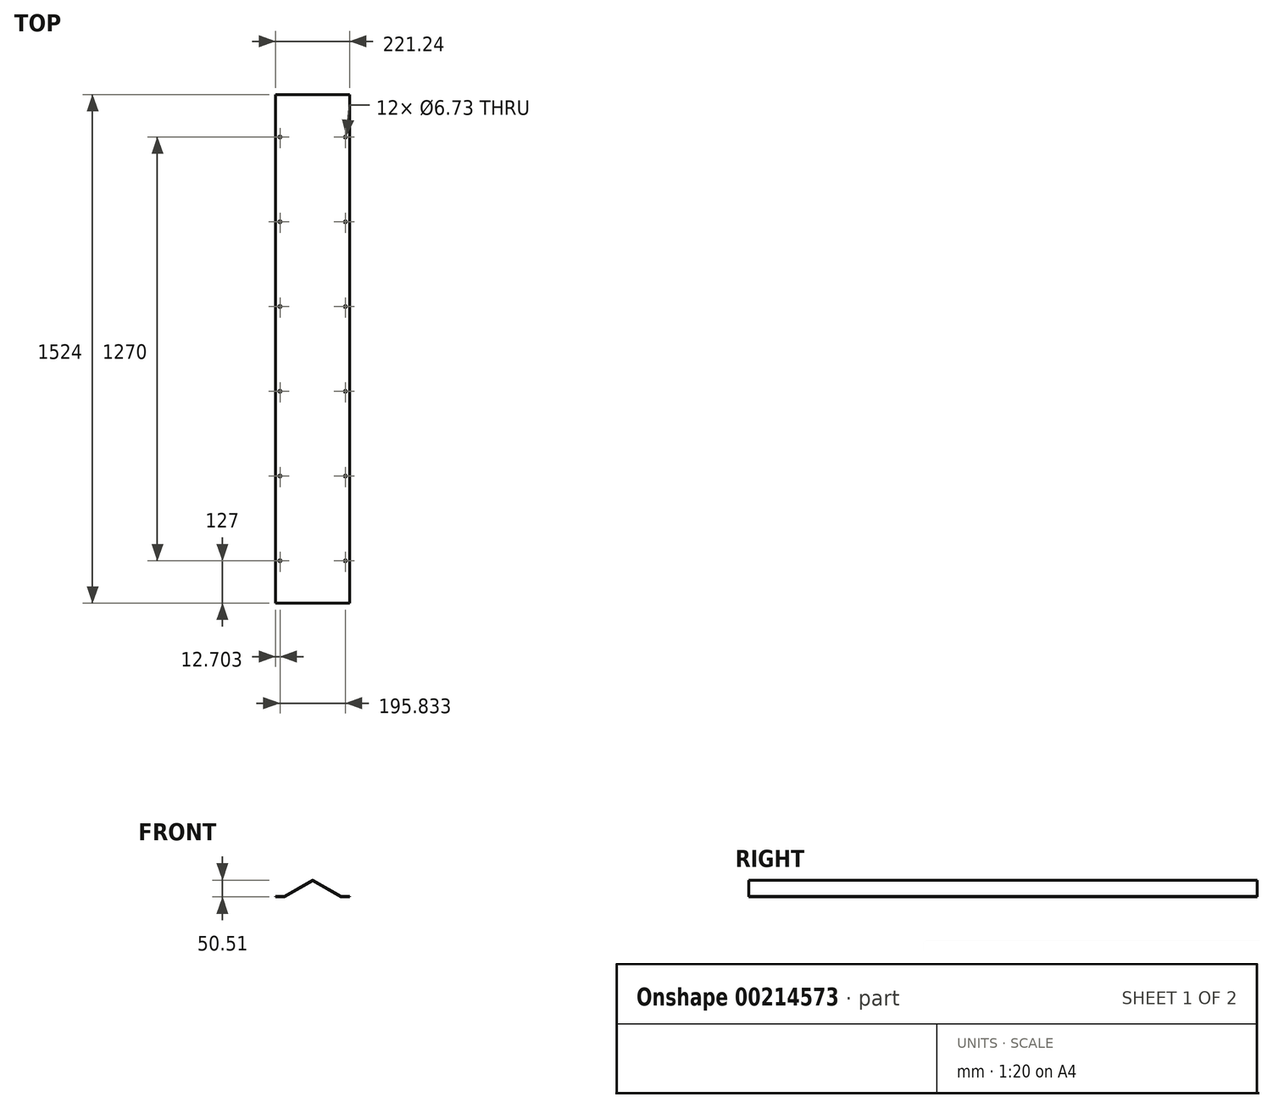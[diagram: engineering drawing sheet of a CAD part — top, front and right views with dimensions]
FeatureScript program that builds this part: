
annotation { "Feature Type Name" : "Feature", "Feature Type Description" : "" }
export const myFeature = defineFeature(function(context is Context, id is Id, definition is map)
    precondition{}
    {
        {
            var Q0;
            Q0=qCreatedBy(makeId("Front.planeOp"),FACE);
            var sketch = newSketch(context, id + "F0", { "sketchPlane" : qUnion([Q0])});
            skLineSegment(sketch, "E0", {"start": v(-0.93, 50.26) * mm, "end": v(-85.16, 1.63) * mm});
            skLineSegment(sketch, "E1", {"start": v(-85.28, 1.6) * mm, "end": v(-110.62, 1.6) * mm});
            skLineSegment(sketch, "E2", {"start": v(0.93, 50.26) * mm, "end": v(85.16, 1.63) * mm});
            skLineSegment(sketch, "E3", {"start": v(85.28, 1.6) * mm, "end": v(110.62, 1.6) * mm});
            skLineSegment(sketch, "E4", {"start": v(-110.62, 1.6) * mm, "end": v(-110.62, 0) * mm});
            skLineSegment(sketch, "E5", {"start": v(-110.62, 0) * mm, "end": v(-85.28, 0) * mm});
            skLineSegment(sketch, "E6", {"start": v(-84.36, 0.25) * mm, "end": v(-0.13, 48.88) * mm});
            skLineSegment(sketch, "E7", {"start": v(0.13, 48.88) * mm, "end": v(84.36, 0.25) * mm});
            skLineSegment(sketch, "E8", {"start": v(110.62, 1.6) * mm, "end": v(110.62, 0) * mm});
            skLineSegment(sketch, "E9", {"start": v(110.62, 0) * mm, "end": v(85.28, 0) * mm});
            skPoint(sketch, "E10.visualSharp", {"position": v(0, 48.95) * mm});
            skArc(sketch, "E10.filletArc", {"start": v(0.13, 48.88) * mm, "mid": v(0, 48.91) * mm, "end": v(-0.13, 48.88) * mm});
            skPoint(sketch, "E11.visualSharp", {"position": v(85.22, 1.6) * mm});
            skArc(sketch, "E11.filletArc", {"start": v(85.16, 1.63) * mm, "mid": v(85.22, 1.6) * mm, "end": v(85.28, 1.6) * mm});
            skPoint(sketch, "E12.visualSharp", {"position": v(-85.22, 1.6) * mm});
            skArc(sketch, "E12.filletArc", {"start": v(-85.28, 1.6) * mm, "mid": v(-85.22, 1.6) * mm, "end": v(-85.16, 1.63) * mm});
            skPoint(sketch, "E13.visualSharp", {"position": v(-84.79, 0) * mm});
            skArc(sketch, "E13.filletArc", {"start": v(-85.28, 0) * mm, "mid": v(-84.8, 0.06) * mm, "end": v(-84.36, 0.25) * mm});
            skPoint(sketch, "E14.visualSharp", {"position": v(0, 50.8) * mm});
            skArc(sketch, "E14.filletArc", {"start": v(0.93, 50.26) * mm, "mid": v(0, 50.51) * mm, "end": v(-0.93, 50.26) * mm});
            skPoint(sketch, "E15.visualSharp", {"position": v(84.79, 0) * mm});
            skArc(sketch, "E15.filletArc", {"start": v(84.36, 0.25) * mm, "mid": v(84.8, 0.06) * mm, "end": v(85.28, 0) * mm});
            skSolve(sketch);
        }
        {
            var Q0;
            Q0 = qSketchRegion(id + "F0", true);
            extrude(context, id + "F1", {"entities" : qUnion([Q0]), "depth" : 1524 * mm});
        }
        {
            var Q0;
            Q0=makeQuery(id+"F1.opExtrude","SWEPT_FACE",FACE,{"disambiguationData":[OSD([sQuery(id+"F0.wireOp",EDGE,"E1")])]});
            var sketch = newSketch(context, id + "F2", { "sketchPlane" : qUnion([Q0])});
            skCircle(sketch, "E16", {"center": v(-97.92, -127) * mm, "radius": 3.37 * mm});
            skCircle(sketch, "E17", {"center": v(97.92, -127) * mm, "radius": 3.37 * mm});
            skCircle(sketch, "E18.0.1.0", {"center": v(-97.92, -381) * mm, "radius": 3.37 * mm});
            skCircle(sketch, "E18.0.1.1", {"center": v(97.92, -381) * mm, "radius": 3.37 * mm});
            skCircle(sketch, "E18.0.2.0", {"center": v(-97.92, -635) * mm, "radius": 3.37 * mm});
            skCircle(sketch, "E18.0.2.1", {"center": v(97.92, -635) * mm, "radius": 3.37 * mm});
            skCircle(sketch, "E18.0.3.0", {"center": v(-97.92, -889) * mm, "radius": 3.37 * mm});
            skCircle(sketch, "E18.0.3.1", {"center": v(97.92, -889) * mm, "radius": 3.37 * mm});
            skCircle(sketch, "E18.0.4.0", {"center": v(-97.92, -1143) * mm, "radius": 3.37 * mm});
            skCircle(sketch, "E18.0.4.1", {"center": v(97.92, -1143) * mm, "radius": 3.37 * mm});
            skCircle(sketch, "E18.0.5.0", {"center": v(-97.92, -1397) * mm, "radius": 3.37 * mm});
            skCircle(sketch, "E18.0.5.1", {"center": v(97.92, -1397) * mm, "radius": 3.37 * mm});
            skCircle(sketch, "E18.1.1.0", {"center": v(-97.92, -381) * mm, "radius": 3.37 * mm});
            skCircle(sketch, "E18.1.1.1", {"center": v(97.92, -381) * mm, "radius": 3.37 * mm});
            skCircle(sketch, "E18.1.2.0", {"center": v(-97.92, -635) * mm, "radius": 3.37 * mm});
            skCircle(sketch, "E18.1.2.1", {"center": v(97.92, -635) * mm, "radius": 3.37 * mm});
            skCircle(sketch, "E18.1.3.0", {"center": v(-97.92, -889) * mm, "radius": 3.37 * mm});
            skCircle(sketch, "E18.1.3.1", {"center": v(97.92, -889) * mm, "radius": 3.37 * mm});
            skCircle(sketch, "E18.1.4.0", {"center": v(-97.92, -1143) * mm, "radius": 3.37 * mm});
            skCircle(sketch, "E18.1.4.1", {"center": v(97.92, -1143) * mm, "radius": 3.37 * mm});
            skCircle(sketch, "E18.1.5.0", {"center": v(-97.92, -1397) * mm, "radius": 3.37 * mm});
            skCircle(sketch, "E18.1.5.1", {"center": v(97.92, -1397) * mm, "radius": 3.37 * mm});
            skCircle(sketch, "E18.2.1.0", {"center": v(-97.92, -381) * mm, "radius": 3.37 * mm});
            skCircle(sketch, "E18.2.1.1", {"center": v(97.92, -381) * mm, "radius": 3.37 * mm});
            skCircle(sketch, "E18.2.2.0", {"center": v(-97.92, -635) * mm, "radius": 3.37 * mm});
            skCircle(sketch, "E18.2.2.1", {"center": v(97.92, -635) * mm, "radius": 3.37 * mm});
            skCircle(sketch, "E18.2.3.0", {"center": v(-97.92, -889) * mm, "radius": 3.37 * mm});
            skCircle(sketch, "E18.2.3.1", {"center": v(97.92, -889) * mm, "radius": 3.37 * mm});
            skCircle(sketch, "E18.2.4.0", {"center": v(-97.92, -1143) * mm, "radius": 3.37 * mm});
            skCircle(sketch, "E18.2.4.1", {"center": v(97.92, -1143) * mm, "radius": 3.37 * mm});
            skCircle(sketch, "E18.2.5.0", {"center": v(-97.92, -1397) * mm, "radius": 3.37 * mm});
            skCircle(sketch, "E18.2.5.1", {"center": v(97.92, -1397) * mm, "radius": 3.37 * mm});
            skLineSegment(sketch, "E18.direction1", {"start": v(-97.92, -127) * mm, "end": v(-97.92, -127) * mm});
            skLineSegment(sketch, "E18.direction2", {"start": v(-97.92, -127) * mm, "end": v(-97.92, -381) * mm, "construction": true});
            skSolve(sketch);
        }
        {
            var Q0;
            Q0 = qSketchRegion(id + "F2", true);
            extrude(context, id + "F3", {"entities" : qUnion([Q0]), "operationType" : NewBodyOperationType.REMOVE, "endBound" : BoundingType.THROUGH_ALL, "oppositeDirection" : true, "depth" : 25.4 * mm});
        }
    });
